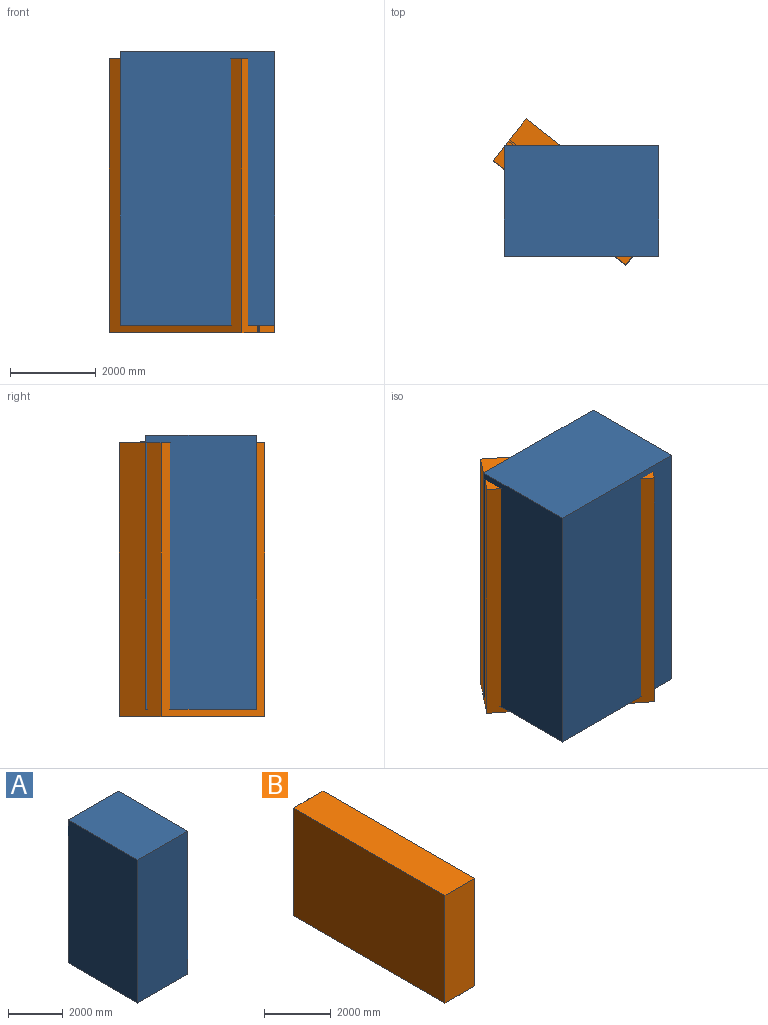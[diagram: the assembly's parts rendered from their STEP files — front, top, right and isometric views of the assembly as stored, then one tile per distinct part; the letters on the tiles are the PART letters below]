
ASSEMBLY  parts=2 mates=2
PART A: 6 faces, bbox 2590.8x3606.8x6400.8 mm
  f0: plane 6400.8x2590.8mm, normal (0,1,0), area 16583192.6mm2, adj f1,f3,f4,f5
  f1: plane 6400.8x3606.8mm, normal (-1,0,0), area 23086405.4mm2, adj f0,f2,f4,f5
  f2: plane 6400.8x2590.8mm, normal (0,-1,0), area 16583192.6mm2, adj f1,f3,f4,f5
  f3: plane 6400.8x3606.8mm, normal (1,0,0), area 23086405.4mm2, adj f0,f2,f4,f5
  f4: plane 3606.8x2590.8mm, normal (0,0,1), area 9344497.4mm2, adj f0,f1,f2,f3
  f5: plane 3606.8x2590.8mm, normal (0,0,-1), area 9344497.4mm2, adj f0,f1,f2,f3
PART B: 15 faces, bbox 1244.6x6426.2x3962.4 mm
  f0: plane 6426.2x622.3mm, normal (0,0,-1), area 3762171.5mm2, adj f4,f6,f7,f8,f9,f10,f11,f12
  f1: plane 3937x622.3mm, normal (0,1,0), area 2449995.1mm2, adj f2,f3,f5,f8
  f2: plane 6400.8x3937mm, normal (-1,0,0), area 25199949.6mm2, adj f1,f3,f5,f6
  f3: plane 6400.8x622.3mm, normal (0,0,-1), area 3983217.8mm2, adj f1,f2,f6,f13
  f4: plane 6400.8x3937mm, normal (1,0,0), area 25199949.6mm2, adj f0,f5,f6,f7
  f5: plane 6426.2x1244.6mm, normal (0,0,1), area 7967639.1mm2, adj f1,f2,f4,f6,f7,f8,f9,f10
  f6: plane 3962.4x1244.6mm, normal (0,-1,0), area 4900597.5mm2, adj f0,f2,f3,f4,f5,f12,f13,f14
  f7: plane 3937x574.92mm, normal (0,1,0), area 2263470.8mm2, adj f0,f4,f5,f9
  f8: plane 3937x25.4mm, normal (-1,0,0), area 99999.8mm2, adj f0,f1,f5,f10
  f9: plane 3937x25.4mm, normal (1,0,0), area 99999.8mm2, adj f0,f5,f7,f10
  f10: plane 3937x47.38mm, normal (0,1,0), area 186524.3mm2, adj f0,f5,f8,f9
  f11: plane 45.53x25.4mm, normal (0,1,0), area 1156.6mm2, adj f0,f12,f13,f14
  f12: plane 6400.8x25.4mm, normal (1,0,0), area 162581.2mm2, adj f0,f6,f11,f14
  f13: plane 6400.8x25.4mm, normal (-1,0,0), area 162580.3mm2, adj f3,f6,f11,f14
  f14: plane 6400.8x45.53mm, normal (0,0,-1), area 222249.7mm2, adj f6,f11,f12,f13
PLACE A rot(axis=(0,0,-1),90deg) t=(0,2590.8,0)mm
PLACE B rot(axis=(0.33,-0.67,-0.67),143.9deg) t=(3.28,784.09,6232.67)mm
MATE parallel A.f5 <-> B.f6  axis (0,0,-1) through (-1803.4,1295.4,0)mm
MATE parallel A.f4 <-> B.f1  axis (0,0,1) through (-1803.4,1295.4,6400.8)mm
